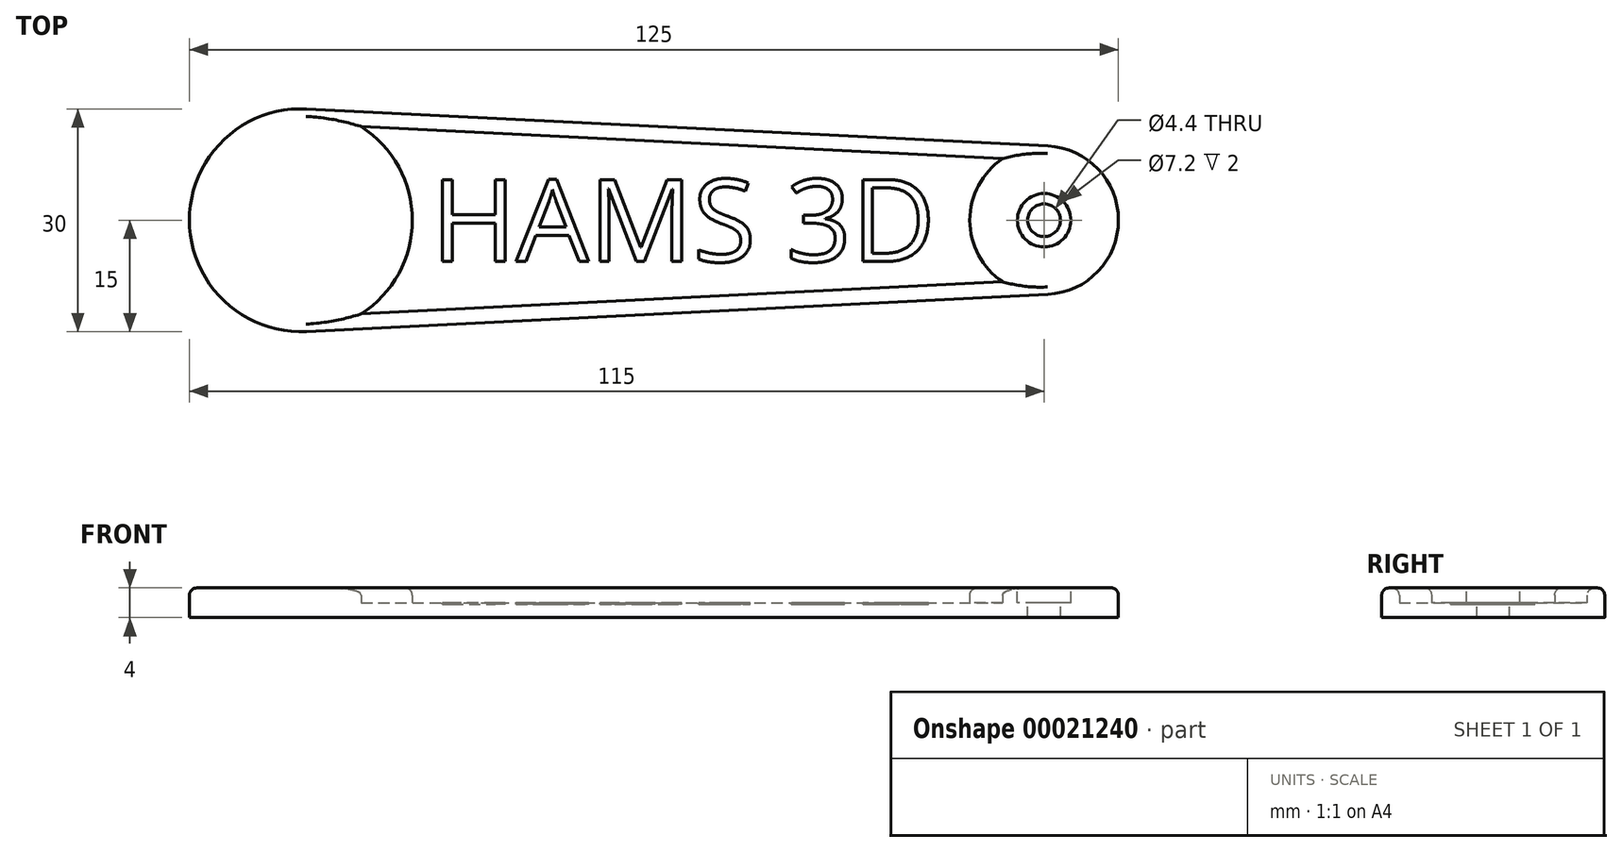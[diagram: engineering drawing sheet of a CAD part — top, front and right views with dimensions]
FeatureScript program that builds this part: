
annotation { "Feature Type Name" : "Feature", "Feature Type Description" : "" }
export const myFeature = defineFeature(function(context is Context, id is Id, definition is map)
    precondition{}
    {
        {
            var Q0;
            Q0=qCreatedBy(makeId("Top.planeOp"),FACE);
            var sketch = newSketch(context, id + "F0", { "sketchPlane" : qUnion([Q0])});
            skCircle(sketch, "E0", {"center": v(0, 0) * mm, "radius": 15 * mm});
            skCircle(sketch, "E1", {"center": v(100, 0) * mm, "radius": 10 * mm});
            skLineSegment(sketch, "E2", {"start": v(0.75, 14.98) * mm, "end": v(100.5, 9.99) * mm});
            skLineSegment(sketch, "E3", {"start": v(0.75, -14.98) * mm, "end": v(100.5, -9.99) * mm});
            skSolve(sketch);
        }
        {
            var Q0;
            {var subQ0=sQuery(id+"F0.wireOp",EDGE,"E1");var subQ2=makeQuery(id+"F0.imprint","INTERSECT",VERTEX,{"derivedFrom":[subQ0,sQuery(id+"F0.wireOp",EDGE,"E2")]});Q0=makeQuery(id+"F0.imprint","IMPRINT",FACE,{"disambiguationData":[TD([[makeQuery(id+"F0.imprint","IMPRINT",EDGE,{"disambiguationData":[TD([[subQ2,-1.0]])],"derivedFrom":subQ0}),1.0]])]});}
            var Q1;
            {var subQ0=sQuery(id+"F0.wireOp",EDGE,"E0");var subQ2=makeQuery(id+"F0.imprint","INTERSECT",VERTEX,{"derivedFrom":[subQ0,sQuery(id+"F0.wireOp",EDGE,"E2")]});Q1=makeQuery(id+"F0.imprint","IMPRINT",FACE,{"disambiguationData":[TD([[makeQuery(id+"F0.imprint","IMPRINT",EDGE,{"disambiguationData":[TD([[subQ2,-1.0]])],"derivedFrom":subQ0}),1.0]])]});}
            var Q2;
            {var subQ1=sQuery(id+"F0.wireOp",EDGE,"E2");Q2=makeQuery(id+"F0.imprint","IMPRINT",FACE,{"disambiguationData":[TD([[makeQuery(id+"F0.imprint","IMPRINT",EDGE,{"derivedFrom":subQ1}),-1.0]])]});}
            extrude(context, id + "F1", {"entities" : qUnion([Q0, Q1, Q2]), "depth" : 4 * mm});
        }
        {
            var Q0;
            Q0=makeQuery(id+"F1.opExtrude","CAP_FACE",FACE,{"disambiguationData":[OSD([sQuery(id+"F0.wireOp",EDGE,"E0"),sQuery(id+"F0.wireOp",EDGE,"E1"),sQuery(id+"F0.wireOp",EDGE,"E2"),sQuery(id+"F0.wireOp",EDGE,"E3")])],"isStart":false});
            shell(context, id + "F2", {"entities" : qUnion([Q0]), "thickness" : 2 * mm});
        }
        {
            var Q0;
            {var subQ0=sQuery(id+"F0.wireOp",EDGE,"E0");var subQ2=makeQuery(id+"F0.imprint","INTERSECT",VERTEX,{"derivedFrom":[subQ0,sQuery(id+"F0.wireOp",EDGE,"E2")]});Q0=makeQuery(id+"F0.imprint","IMPRINT",FACE,{"disambiguationData":[TD([[makeQuery(id+"F0.imprint","IMPRINT",EDGE,{"disambiguationData":[TD([[subQ2,-1.0]])],"derivedFrom":subQ0}),1.0]])]});}
            var Q1;
            {var subQ0=sQuery(id+"F0.wireOp",EDGE,"E1");var subQ2=makeQuery(id+"F0.imprint","INTERSECT",VERTEX,{"derivedFrom":[subQ0,sQuery(id+"F0.wireOp",EDGE,"E2")]});Q1=makeQuery(id+"F0.imprint","IMPRINT",FACE,{"disambiguationData":[TD([[makeQuery(id+"F0.imprint","IMPRINT",EDGE,{"disambiguationData":[TD([[subQ2,-1.0]])],"derivedFrom":subQ0}),1.0]])]});}
            extrude(context, id + "F3", {"entities" : qUnion([Q0, Q1]), "operationType" : NewBodyOperationType.ADD, "depth" : 4 * mm});
        }
        {
            var Q0;
            {var subQ0=sQuery(id+"F0.wireOp",EDGE,"E3");Q0=makeQuery(id+"F2.opShell","OFFSET_EDGE",EDGE,{"disambiguationData":[OSD([subQ0]),TDD([makeQuery(id+"F1.opExtrude","CAP_EDGE",EDGE,{"disambiguationData":[OSD([subQ0])],"isStart":false})])]});}
            var Q1;
            {var subQ0=sQuery(id+"F0.wireOp",EDGE,"E0");var subQ1=sQuery(id+"F0.wireOp",EDGE,"E1");Q1=makeQuery(id+"F3.boolean.opBoolean","MERGE",FACE,{"derivedFrom":[makeQuery(id+"F1.opExtrude","CAP_FACE",FACE,{"disambiguationData":[OSD([subQ0,subQ1,sQuery(id+"F0.wireOp",EDGE,"E2"),sQuery(id+"F0.wireOp",EDGE,"E3")])],"isStart":false}),makeQuery(id+"F3.opExtrude","CAP_FACE",FACE,{"disambiguationData":[OSD([subQ0])],"isStart":false}),makeQuery(id+"F3.opExtrude","CAP_FACE",FACE,{"disambiguationData":[OSD([subQ1])],"isStart":false})]});}
            fillet(context, id + "F4", {"entities" : qUnion([Q0, Q1]), "radius" : 1 * mm, "tangentPropagation" : true, "allowEdgeOverflow" : false});
        }
        {
            var Q0;
            {var subQ0=sQuery(id+"F0.wireOp",EDGE,"E0");var subQ1=sQuery(id+"F0.wireOp",EDGE,"E1");Q0=makeQuery(id+"F4.opFillet","SPLIT",FACE,{"disambiguationData":[OD(1.0)],"derivedFrom":makeQuery(id+"F3.boolean.opBoolean","MERGE",FACE,{"derivedFrom":[makeQuery(id+"F1.opExtrude","CAP_FACE",FACE,{"disambiguationData":[OSD([subQ0,subQ1,sQuery(id+"F0.wireOp",EDGE,"E2"),sQuery(id+"F0.wireOp",EDGE,"E3")])],"isStart":false}),makeQuery(id+"F3.opExtrude","CAP_FACE",FACE,{"disambiguationData":[OSD([subQ0])],"isStart":false}),makeQuery(id+"F3.opExtrude","CAP_FACE",FACE,{"disambiguationData":[OSD([subQ1])],"isStart":false})]})});}
            var sketch = newSketch(context, id + "F5", { "sketchPlane" : qUnion([Q0])});
            skCircle(sketch, "E4", {"center": v(100, 0) * mm, "radius": 2.2 * mm});
            skCircle(sketch, "E5", {"center": v(100, 0) * mm, "radius": 3.6 * mm});
            skSolve(sketch);
        }
        {
            var Q0;
            Q0=makeQuery(id+"F5.imprint","IMPRINT",FACE,{"disambiguationData":[TD([[makeQuery(id+"F5.imprint","IMPRINT",EDGE,{"derivedFrom":sQuery(id+"F5.wireOp",EDGE,"E4")}),1.0]])]});
            extrude(context, id + "F6", {"entities" : qUnion([Q0]), "operationType" : NewBodyOperationType.REMOVE, "endBound" : BoundingType.UP_TO_NEXT, "oppositeDirection" : true, "depth" : 25 * mm});
        }
        {
            var Q0;
            Q0=makeQuery(id+"F5.imprint","IMPRINT",FACE,{"disambiguationData":[TD([[makeQuery(id+"F5.imprint","IMPRINT",EDGE,{"derivedFrom":sQuery(id+"F5.wireOp",EDGE,"E4")}),-1.0]])]});
            extrude(context, id + "F7", {"entities" : qUnion([Q0]), "operationType" : NewBodyOperationType.REMOVE, "oppositeDirection" : true, "depth" : 2 * mm});
        }
        {
            var Q0;
            Q0=makeQuery(id+"F2.opShell","OFFSET_FACE",FACE,{"disambiguationData":[OSD([sQuery(id+"F0.wireOp",EDGE,"E0"),sQuery(id+"F0.wireOp",EDGE,"E1"),sQuery(id+"F0.wireOp",EDGE,"E2"),sQuery(id+"F0.wireOp",EDGE,"E3")])]});
            var sketch = newSketch(context, id + "F8", { "sketchPlane" : qUnion([Q0])});
            skText(sketch, "E6", { "text": "HAMS 3D", "fontName": "OpenSans-Regular.ttf"});
            skLineSegment(sketch, "E7", {"start": v(100, 0) * mm, "end": v(0, 0) * mm, "construction": true});
            const initialGuessF8  = {"E6": [0.01755, -0.00557, 1, 0, 0.01114]};
            skSetInitialGuess(sketch, initialGuessF8);
            skSolve(sketch);
        }
        {
            var Q0;
            Q0 = qSketchRegion(id + "F8", true);
            extrude(context, id + "F9", {"entities" : qUnion([Q0]), "operationType" : NewBodyOperationType.REMOVE, "oppositeDirection" : true, "depth" : 0.2 * mm});
        }
    });
